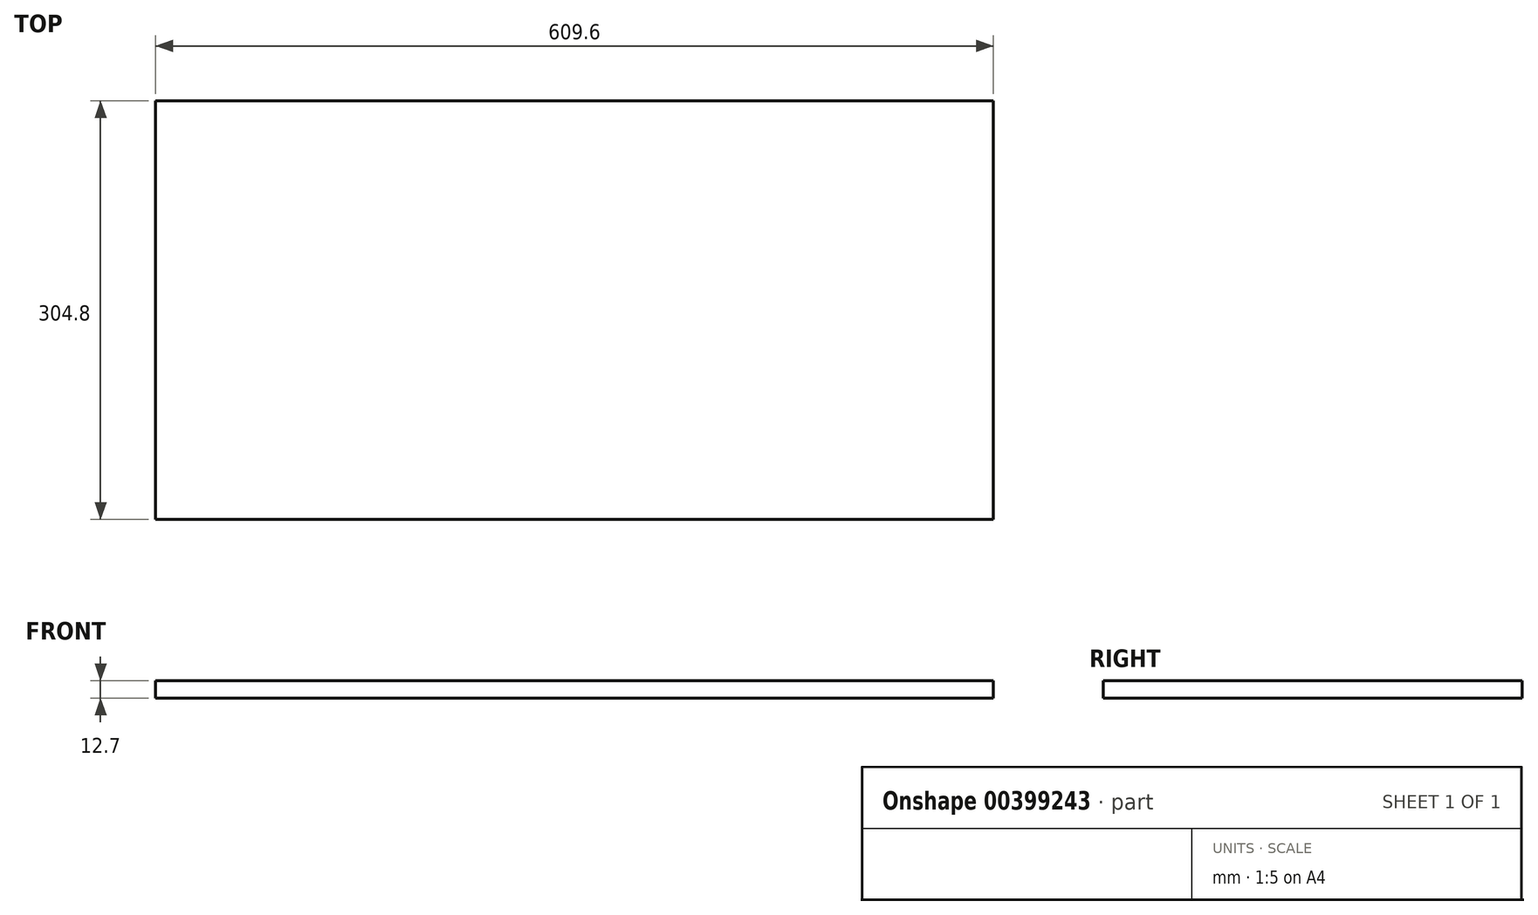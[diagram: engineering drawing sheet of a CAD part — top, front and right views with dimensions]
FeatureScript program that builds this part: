
annotation { "Feature Type Name" : "Feature", "Feature Type Description" : "" }
export const myFeature = defineFeature(function(context is Context, id is Id, definition is map)
    precondition{}
    {
        {
            var Q0;
            Q0=qCreatedBy(makeId("Top.planeOp"),FACE);
            var sketch = newSketch(context, id + "F0", { "sketchPlane" : qUnion([Q0])});
            skLineSegment(sketch, "E0.bottom", {"start": v(-289.62, -165.78) * mm, "end": v(319.98, -165.78) * mm});
            skLineSegment(sketch, "E0.top", {"start": v(-289.62, 139.02) * mm, "end": v(319.98, 139.02) * mm});
            skLineSegment(sketch, "E0.left", {"start": v(-289.62, -165.78) * mm, "end": v(-289.62, 139.02) * mm});
            skLineSegment(sketch, "E0.right", {"start": v(319.98, -165.78) * mm, "end": v(319.98, 139.02) * mm});
            skSolve(sketch);
        }
        {
            var Q0;
            Q0 = qSketchRegion(id + "F0", true);
            extrude(context, id + "F1", {"entities" : qUnion([Q0]), "depth" : 12.7 * mm});
        }
    });
